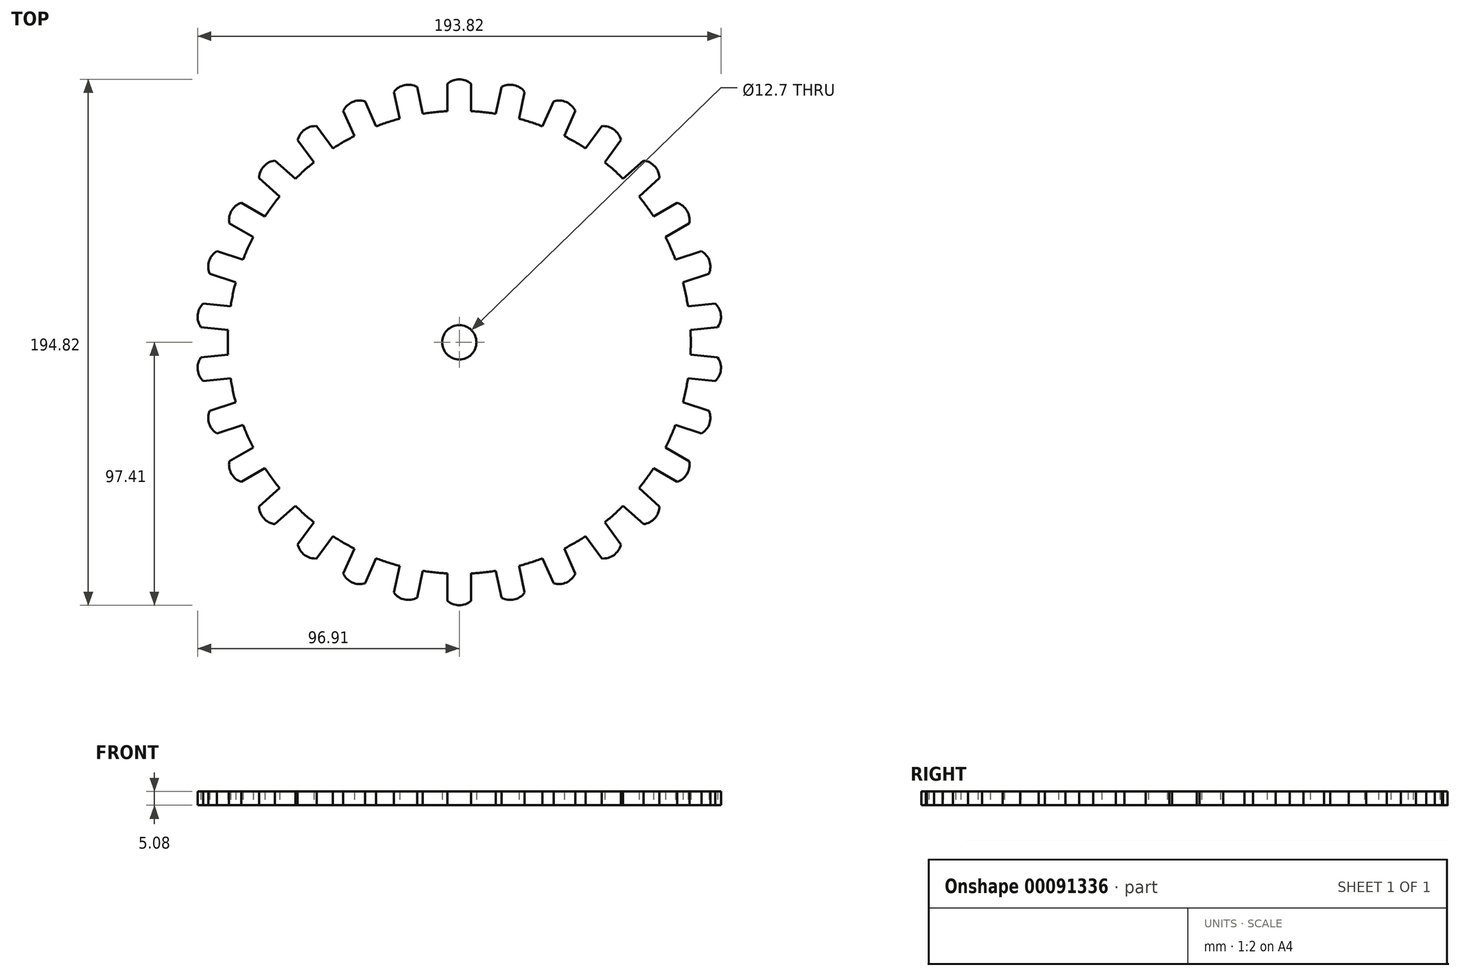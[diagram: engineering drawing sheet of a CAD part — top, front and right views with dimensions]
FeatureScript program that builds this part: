
annotation { "Feature Type Name" : "Feature", "Feature Type Description" : "" }
export const myFeature = defineFeature(function(context is Context, id is Id, definition is map)
    precondition{}
    {
        {
            var Q0;
            Q0=qCreatedBy(makeId("Top.planeOp"),FACE);
            var sketch = newSketch(context, id + "F0", { "sketchPlane" : qUnion([Q0])});
            skArc(sketch, "E0", {"start": v(-4.4, 85.61) * mm, "mid": v(-8.96, 85.26) * mm, "end": v(-13.5, 84.65) * mm});
            skLineSegment(sketch, "E1.left", {"start": v(4.4, 85.61) * mm, "end": v(4.4, 95.77) * mm});
            skLineSegment(sketch, "E1.right", {"start": v(-4.4, 85.61) * mm, "end": v(-4.4, 95.77) * mm});
            skArc(sketch, "E2", {"start": v(4.4, 95.77) * mm, "mid": v(0, 97.4) * mm, "end": v(-4.4, 95.77) * mm});
            skPoint(sketch, "E3.start.orphan", {"position": v(0, 95.77) * mm});
            skLineSegment(sketch, "E4.1.0", {"start": v(-13.5, 84.65) * mm, "end": v(-15.62, 94.6) * mm});
            skArc(sketch, "E4.1.1", {"start": v(-15.62, 94.6) * mm, "mid": v(-20.25, 95.28) * mm, "end": v(-24.2, 92.77) * mm});
            skLineSegment(sketch, "E4.1.2", {"start": v(-22.1, 82.83) * mm, "end": v(-24.2, 92.77) * mm});
            skLineSegment(sketch, "E4.2.0", {"start": v(-30.8, 80) * mm, "end": v(-34.94, 89.28) * mm});
            skArc(sketch, "E4.2.1", {"start": v(-34.94, 89.28) * mm, "mid": v(-39.62, 88.99) * mm, "end": v(-42.97, 85.7) * mm});
            skLineSegment(sketch, "E4.2.2", {"start": v(-38.83, 76.42) * mm, "end": v(-42.97, 85.7) * mm});
            skLineSegment(sketch, "E4.3.0", {"start": v(-46.77, 71.84) * mm, "end": v(-52.74, 80.06) * mm});
            skArc(sketch, "E4.3.1", {"start": v(-52.74, 80.06) * mm, "mid": v(-57.25, 78.8) * mm, "end": v(-59.85, 74.9) * mm});
            skLineSegment(sketch, "E4.3.2", {"start": v(-53.87, 66.68) * mm, "end": v(-59.85, 74.9) * mm});
            skLineSegment(sketch, "E4.4.0", {"start": v(-60.68, 60.55) * mm, "end": v(-68.23, 67.35) * mm});
            skArc(sketch, "E4.4.1", {"start": v(-68.23, 67.35) * mm, "mid": v(-72.39, 65.18) * mm, "end": v(-74.11, 60.82) * mm});
            skLineSegment(sketch, "E4.4.2", {"start": v(-66.56, 54.02) * mm, "end": v(-74.11, 60.82) * mm});
            skLineSegment(sketch, "E4.5.0", {"start": v(-71.95, 46.6) * mm, "end": v(-80.75, 51.69) * mm});
            skArc(sketch, "E4.5.1", {"start": v(-80.75, 51.69) * mm, "mid": v(-84.36, 48.7) * mm, "end": v(-85.14, 44.08) * mm});
            skLineSegment(sketch, "E4.5.2", {"start": v(-76.34, 39) * mm, "end": v(-85.14, 44.08) * mm});
            skLineSegment(sketch, "E4.6.0", {"start": v(-80.07, 30.63) * mm, "end": v(-89.73, 33.77) * mm});
            skArc(sketch, "E4.6.1", {"start": v(-89.73, 33.77) * mm, "mid": v(-92.64, 30.1) * mm, "end": v(-92.44, 25.42) * mm});
            skLineSegment(sketch, "E4.6.2", {"start": v(-82.78, 22.28) * mm, "end": v(-92.44, 25.42) * mm});
            skLineSegment(sketch, "E4.7.0", {"start": v(-84.68, 13.32) * mm, "end": v(-94.79, 14.38) * mm});
            skArc(sketch, "E4.7.1", {"start": v(-94.79, 14.38) * mm, "mid": v(-96.87, 10.18) * mm, "end": v(-95.7, 5.64) * mm});
            skLineSegment(sketch, "E4.7.2", {"start": v(-85.6, 4.58) * mm, "end": v(-95.7, 5.64) * mm});
            skLineSegment(sketch, "E4.8.0", {"start": v(-85.6, -4.58) * mm, "end": v(-95.7, -5.64) * mm});
            skArc(sketch, "E4.8.1", {"start": v(-95.7, -5.64) * mm, "mid": v(-96.87, -10.18) * mm, "end": v(-94.79, -14.38) * mm});
            skLineSegment(sketch, "E4.8.2", {"start": v(-84.68, -13.32) * mm, "end": v(-94.79, -14.38) * mm});
            skLineSegment(sketch, "E4.9.0", {"start": v(-82.78, -22.28) * mm, "end": v(-92.44, -25.42) * mm});
            skArc(sketch, "E4.9.1", {"start": v(-92.44, -25.42) * mm, "mid": v(-92.64, -30.1) * mm, "end": v(-89.73, -33.77) * mm});
            skLineSegment(sketch, "E4.9.2", {"start": v(-80.07, -30.63) * mm, "end": v(-89.73, -33.77) * mm});
            skLineSegment(sketch, "E4.10.0", {"start": v(-76.34, -39) * mm, "end": v(-85.14, -44.08) * mm});
            skArc(sketch, "E4.10.1", {"start": v(-85.14, -44.08) * mm, "mid": v(-84.36, -48.7) * mm, "end": v(-80.75, -51.69) * mm});
            skLineSegment(sketch, "E4.10.2", {"start": v(-71.95, -46.6) * mm, "end": v(-80.75, -51.69) * mm});
            skLineSegment(sketch, "E4.11.0", {"start": v(-66.56, -54.02) * mm, "end": v(-74.11, -60.82) * mm});
            skArc(sketch, "E4.11.1", {"start": v(-74.11, -60.82) * mm, "mid": v(-72.39, -65.18) * mm, "end": v(-68.23, -67.35) * mm});
            skLineSegment(sketch, "E4.11.2", {"start": v(-60.68, -60.55) * mm, "end": v(-68.23, -67.35) * mm});
            skLineSegment(sketch, "E4.12.0", {"start": v(-53.87, -66.68) * mm, "end": v(-59.85, -74.9) * mm});
            skArc(sketch, "E4.12.1", {"start": v(-59.85, -74.9) * mm, "mid": v(-57.25, -78.8) * mm, "end": v(-52.74, -80.06) * mm});
            skLineSegment(sketch, "E4.12.2", {"start": v(-46.77, -71.84) * mm, "end": v(-52.74, -80.06) * mm});
            skLineSegment(sketch, "E4.13.0", {"start": v(-38.83, -76.42) * mm, "end": v(-42.97, -85.7) * mm});
            skArc(sketch, "E4.13.1", {"start": v(-42.97, -85.7) * mm, "mid": v(-39.62, -88.99) * mm, "end": v(-34.94, -89.28) * mm});
            skLineSegment(sketch, "E4.13.2", {"start": v(-30.8, -80) * mm, "end": v(-34.94, -89.28) * mm});
            skLineSegment(sketch, "E4.14.0", {"start": v(-22.1, -82.83) * mm, "end": v(-24.2, -92.77) * mm});
            skArc(sketch, "E4.14.1", {"start": v(-24.2, -92.77) * mm, "mid": v(-20.25, -95.28) * mm, "end": v(-15.62, -94.6) * mm});
            skLineSegment(sketch, "E4.14.2", {"start": v(-13.5, -84.65) * mm, "end": v(-15.62, -94.6) * mm});
            skLineSegment(sketch, "E4.15.0", {"start": v(-4.4, -85.61) * mm, "end": v(-4.4, -95.77) * mm});
            skArc(sketch, "E4.15.1", {"start": v(-4.4, -95.77) * mm, "mid": v(0, -97.4) * mm, "end": v(4.4, -95.77) * mm});
            skLineSegment(sketch, "E4.15.2", {"start": v(4.4, -85.61) * mm, "end": v(4.4, -95.77) * mm});
            skLineSegment(sketch, "E4.16.0", {"start": v(13.5, -84.65) * mm, "end": v(15.62, -94.6) * mm});
            skArc(sketch, "E4.16.1", {"start": v(15.62, -94.6) * mm, "mid": v(20.25, -95.28) * mm, "end": v(24.2, -92.77) * mm});
            skLineSegment(sketch, "E4.16.2", {"start": v(22.1, -82.83) * mm, "end": v(24.2, -92.77) * mm});
            skLineSegment(sketch, "E4.17.0", {"start": v(30.8, -80) * mm, "end": v(34.94, -89.28) * mm});
            skArc(sketch, "E4.17.1", {"start": v(34.94, -89.28) * mm, "mid": v(39.62, -88.99) * mm, "end": v(42.97, -85.7) * mm});
            skLineSegment(sketch, "E4.17.2", {"start": v(38.83, -76.42) * mm, "end": v(42.97, -85.7) * mm});
            skLineSegment(sketch, "E4.18.0", {"start": v(46.77, -71.84) * mm, "end": v(52.74, -80.06) * mm});
            skArc(sketch, "E4.18.1", {"start": v(52.74, -80.06) * mm, "mid": v(57.25, -78.8) * mm, "end": v(59.85, -74.9) * mm});
            skLineSegment(sketch, "E4.18.2", {"start": v(53.87, -66.68) * mm, "end": v(59.85, -74.9) * mm});
            skLineSegment(sketch, "E4.19.0", {"start": v(60.68, -60.55) * mm, "end": v(68.23, -67.35) * mm});
            skArc(sketch, "E4.19.1", {"start": v(68.23, -67.35) * mm, "mid": v(72.39, -65.18) * mm, "end": v(74.11, -60.82) * mm});
            skLineSegment(sketch, "E4.19.2", {"start": v(66.56, -54.02) * mm, "end": v(74.11, -60.82) * mm});
            skLineSegment(sketch, "E4.20.0", {"start": v(71.95, -46.6) * mm, "end": v(80.75, -51.69) * mm});
            skArc(sketch, "E4.20.1", {"start": v(80.75, -51.69) * mm, "mid": v(84.36, -48.7) * mm, "end": v(85.14, -44.08) * mm});
            skLineSegment(sketch, "E4.20.2", {"start": v(76.34, -39) * mm, "end": v(85.14, -44.08) * mm});
            skLineSegment(sketch, "E4.21.0", {"start": v(80.07, -30.63) * mm, "end": v(89.73, -33.77) * mm});
            skArc(sketch, "E4.21.1", {"start": v(89.73, -33.77) * mm, "mid": v(92.64, -30.1) * mm, "end": v(92.44, -25.42) * mm});
            skLineSegment(sketch, "E4.21.2", {"start": v(82.78, -22.28) * mm, "end": v(92.44, -25.42) * mm});
            skLineSegment(sketch, "E4.22.0", {"start": v(84.68, -13.32) * mm, "end": v(94.79, -14.38) * mm});
            skArc(sketch, "E4.22.1", {"start": v(94.79, -14.38) * mm, "mid": v(96.87, -10.18) * mm, "end": v(95.7, -5.64) * mm});
            skLineSegment(sketch, "E4.22.2", {"start": v(85.6, -4.58) * mm, "end": v(95.7, -5.64) * mm});
            skLineSegment(sketch, "E4.23.0", {"start": v(85.6, 4.58) * mm, "end": v(95.7, 5.64) * mm});
            skArc(sketch, "E4.23.1", {"start": v(95.7, 5.64) * mm, "mid": v(96.87, 10.18) * mm, "end": v(94.79, 14.38) * mm});
            skLineSegment(sketch, "E4.23.2", {"start": v(84.68, 13.32) * mm, "end": v(94.79, 14.38) * mm});
            skLineSegment(sketch, "E4.24.0", {"start": v(82.78, 22.28) * mm, "end": v(92.44, 25.42) * mm});
            skArc(sketch, "E4.24.1", {"start": v(92.44, 25.42) * mm, "mid": v(92.64, 30.1) * mm, "end": v(89.73, 33.77) * mm});
            skLineSegment(sketch, "E4.24.2", {"start": v(80.07, 30.63) * mm, "end": v(89.73, 33.77) * mm});
            skLineSegment(sketch, "E4.25.0", {"start": v(76.34, 39) * mm, "end": v(85.14, 44.08) * mm});
            skArc(sketch, "E4.25.1", {"start": v(85.14, 44.08) * mm, "mid": v(84.36, 48.7) * mm, "end": v(80.75, 51.69) * mm});
            skLineSegment(sketch, "E4.25.2", {"start": v(71.95, 46.6) * mm, "end": v(80.75, 51.69) * mm});
            skLineSegment(sketch, "E4.26.0", {"start": v(66.56, 54.02) * mm, "end": v(74.11, 60.82) * mm});
            skArc(sketch, "E4.26.1", {"start": v(74.11, 60.82) * mm, "mid": v(72.39, 65.18) * mm, "end": v(68.23, 67.35) * mm});
            skLineSegment(sketch, "E4.26.2", {"start": v(60.68, 60.55) * mm, "end": v(68.23, 67.35) * mm});
            skLineSegment(sketch, "E4.27.0", {"start": v(53.87, 66.68) * mm, "end": v(59.85, 74.9) * mm});
            skArc(sketch, "E4.27.1", {"start": v(59.85, 74.9) * mm, "mid": v(57.25, 78.8) * mm, "end": v(52.74, 80.06) * mm});
            skLineSegment(sketch, "E4.27.2", {"start": v(46.77, 71.84) * mm, "end": v(52.74, 80.06) * mm});
            skLineSegment(sketch, "E4.28.0", {"start": v(38.83, 76.42) * mm, "end": v(42.97, 85.7) * mm});
            skArc(sketch, "E4.28.1", {"start": v(42.97, 85.7) * mm, "mid": v(39.62, 88.99) * mm, "end": v(34.94, 89.28) * mm});
            skLineSegment(sketch, "E4.28.2", {"start": v(30.8, 80) * mm, "end": v(34.94, 89.28) * mm});
            skLineSegment(sketch, "E4.29.0", {"start": v(22.1, 82.83) * mm, "end": v(24.2, 92.77) * mm});
            skArc(sketch, "E4.29.1", {"start": v(24.2, 92.77) * mm, "mid": v(20.25, 95.28) * mm, "end": v(15.62, 94.6) * mm});
            skLineSegment(sketch, "E4.29.2", {"start": v(13.5, 84.65) * mm, "end": v(15.62, 94.6) * mm});
            skArc(sketch, "E5.trimOffspring", {"start": v(-22.1, 82.83) * mm, "mid": v(-26.5, 81.53) * mm, "end": v(-30.8, 80) * mm});
            skArc(sketch, "E6.trimOffspring", {"start": v(-38.83, 76.42) * mm, "mid": v(-42.86, 74.24) * mm, "end": v(-46.77, 71.84) * mm});
            skArc(sketch, "E7.trimOffspring", {"start": v(-53.87, 66.68) * mm, "mid": v(-57.36, 63.7) * mm, "end": v(-60.68, 60.55) * mm});
            skArc(sketch, "E8.trimOffspring", {"start": v(-66.56, 54.02) * mm, "mid": v(-69.35, 50.39) * mm, "end": v(-71.95, 46.6) * mm});
            skArc(sketch, "E9.trimOffspring", {"start": v(-76.34, 39) * mm, "mid": v(-78.31, 34.87) * mm, "end": v(-80.07, 30.63) * mm});
            skArc(sketch, "E10.trimOffspring", {"start": v(-82.78, 22.28) * mm, "mid": v(-83.85, 17.82) * mm, "end": v(-84.68, 13.32) * mm});
            skArc(sketch, "E11.trimOffspring", {"start": v(-85.6, 4.58) * mm, "mid": v(-85.73, 0) * mm, "end": v(-85.6, -4.58) * mm});
            skArc(sketch, "E12.trimOffspring", {"start": v(-84.68, -13.32) * mm, "mid": v(-83.85, -17.82) * mm, "end": v(-82.78, -22.28) * mm});
            skArc(sketch, "E13.trimOffspring", {"start": v(-80.07, -30.63) * mm, "mid": v(-78.31, -34.87) * mm, "end": v(-76.34, -39) * mm});
            skArc(sketch, "E14.trimOffspring", {"start": v(-71.95, -46.6) * mm, "mid": v(-69.35, -50.39) * mm, "end": v(-66.56, -54.02) * mm});
            skArc(sketch, "E15.trimOffspring", {"start": v(-30.8, -80) * mm, "mid": v(-26.5, -81.53) * mm, "end": v(-22.1, -82.83) * mm});
            skArc(sketch, "E16.trimOffspring", {"start": v(-46.77, -71.84) * mm, "mid": v(-42.86, -74.24) * mm, "end": v(-38.83, -76.42) * mm});
            skArc(sketch, "E17.trimOffspring", {"start": v(-60.68, -60.55) * mm, "mid": v(-57.36, -63.7) * mm, "end": v(-53.87, -66.68) * mm});
            skArc(sketch, "E18.trimOffspring", {"start": v(-13.5, -84.65) * mm, "mid": v(-8.96, -85.26) * mm, "end": v(-4.4, -85.61) * mm});
            skArc(sketch, "E19.trimOffspring", {"start": v(4.4, -85.61) * mm, "mid": v(8.96, -85.26) * mm, "end": v(13.5, -84.65) * mm});
            skArc(sketch, "E20.trimOffspring", {"start": v(22.1, -82.83) * mm, "mid": v(26.5, -81.53) * mm, "end": v(30.8, -80) * mm});
            skArc(sketch, "E21.trimOffspring", {"start": v(38.83, -76.42) * mm, "mid": v(42.86, -74.24) * mm, "end": v(46.77, -71.84) * mm});
            skArc(sketch, "E22.trimOffspring", {"start": v(53.87, -66.68) * mm, "mid": v(57.36, -63.7) * mm, "end": v(60.68, -60.55) * mm});
            skArc(sketch, "E23.trimOffspring", {"start": v(66.56, -54.02) * mm, "mid": v(69.35, -50.39) * mm, "end": v(71.95, -46.6) * mm});
            skArc(sketch, "E24.trimOffspring", {"start": v(76.34, -39) * mm, "mid": v(78.31, -34.87) * mm, "end": v(80.07, -30.63) * mm});
            skArc(sketch, "E25.trimOffspring", {"start": v(82.78, -22.28) * mm, "mid": v(83.85, -17.82) * mm, "end": v(84.68, -13.32) * mm});
            skArc(sketch, "E26.trimOffspring", {"start": v(85.6, -4.58) * mm, "mid": v(85.73, 0) * mm, "end": v(85.6, 4.58) * mm});
            skArc(sketch, "E27.trimOffspring", {"start": v(84.68, 13.32) * mm, "mid": v(83.85, 17.82) * mm, "end": v(82.78, 22.28) * mm});
            skArc(sketch, "E28.trimOffspring", {"start": v(80.07, 30.63) * mm, "mid": v(78.31, 34.87) * mm, "end": v(76.34, 39) * mm});
            skArc(sketch, "E29.trimOffspring", {"start": v(60.68, 60.55) * mm, "mid": v(57.36, 63.7) * mm, "end": v(53.87, 66.68) * mm});
            skArc(sketch, "E30.trimOffspring", {"start": v(46.77, 71.84) * mm, "mid": v(42.86, 74.24) * mm, "end": v(38.83, 76.42) * mm});
            skArc(sketch, "E31.trimOffspring", {"start": v(30.8, 80) * mm, "mid": v(26.5, 81.53) * mm, "end": v(22.1, 82.83) * mm});
            skArc(sketch, "E32.trimOffspring", {"start": v(13.5, 84.65) * mm, "mid": v(8.96, 85.26) * mm, "end": v(4.4, 85.61) * mm});
            skCircle(sketch, "E33", {"center": v(0, 0) * mm, "radius": 6.35 * mm});
            skArc(sketch, "E34.trimOffspring", {"start": v(71.95, 46.6) * mm, "mid": v(69.35, 50.39) * mm, "end": v(66.56, 54.02) * mm});
            skSolve(sketch);
        }
        {
            var Q0;
            Q0=makeQuery(id+"F0.imprint","IMPRINT",FACE,{"disambiguationData":[TD([[makeQuery(id+"F0.imprint","IMPRINT",EDGE,{"derivedFrom":sQuery(id+"F0.wireOp",EDGE,"E0")}),1.0]])]});
            extrude(context, id + "F1", {"entities" : qUnion([Q0]), "depth" : 5.08 * mm});
        }
    });
